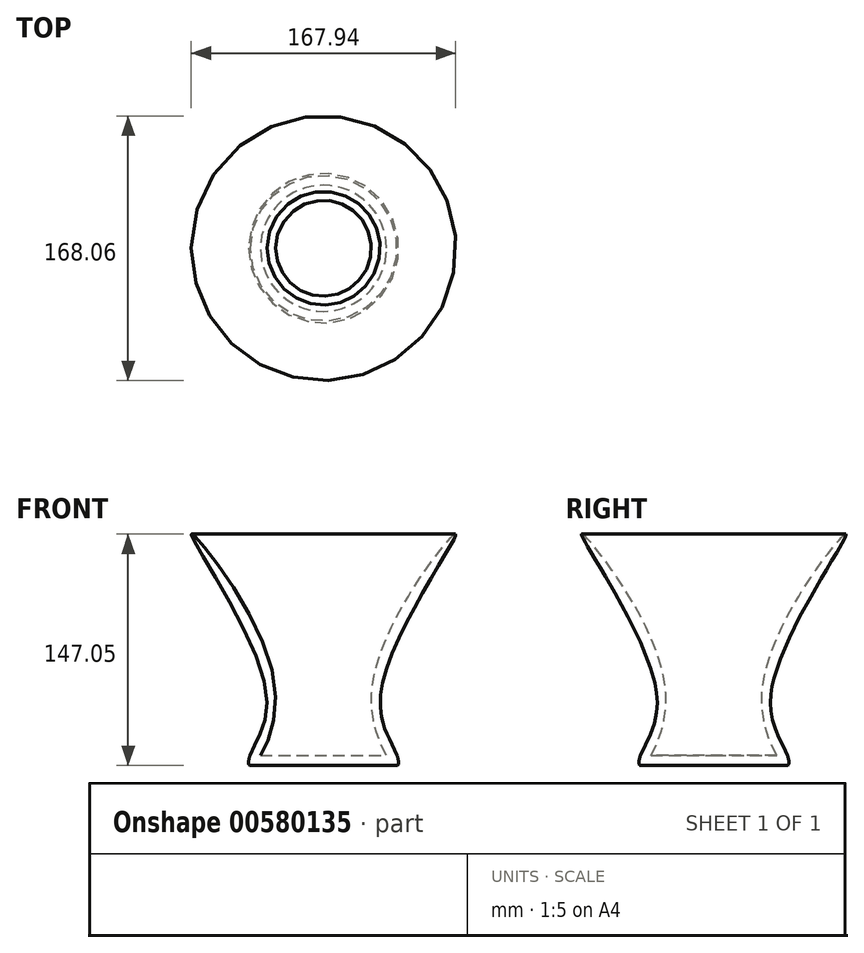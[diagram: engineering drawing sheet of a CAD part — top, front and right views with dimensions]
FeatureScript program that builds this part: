
annotation { "Feature Type Name" : "Feature", "Feature Type Description" : "" }
export const myFeature = defineFeature(function(context is Context, id is Id, definition is map)
    precondition{}
    {
        {
            var Q0;
            Q0=qCreatedBy(makeId("Front.planeOp"),FACE);
            var sketch = newSketch(context, id + "F0", { "sketchPlane" : qUnion([Q0])});
            skLineSegment(sketch, "E0", {"start": v(0, 0) * mm, "end": v(0, 59.79) * mm});
            skLineSegment(sketch, "E1", {"start": v(0, 0) * mm, "end": v(46.65, 0) * mm});
            skFitSpline(sketch, "E2", {"points": [v(46.65, 0) * mm, v(31.07, 51.58) * mm, v(84, 146.97) * mm, v(36.89, 49.84) * mm, v(46.65, 6.58) * mm, v(46.65, 0) * mm]});
            skLineSegment(sketch, "E3", {"start": v(46.65, 6.58) * mm, "end": v(0, 6.58) * mm});
            skSolve(sketch);
        }
        {
            var Q0;
            Q0 = qSketchRegion(id + "F0", true);
            var Q1;
            Q1=sQuery(id+"F0.wireOp",EDGE,"E0");
            revolve(context, id + "F1", {"entities" : qUnion([Q0]), "axis" : qUnion([Q1]), "revolveType" : RevolveType.FULL});
        }
    });
